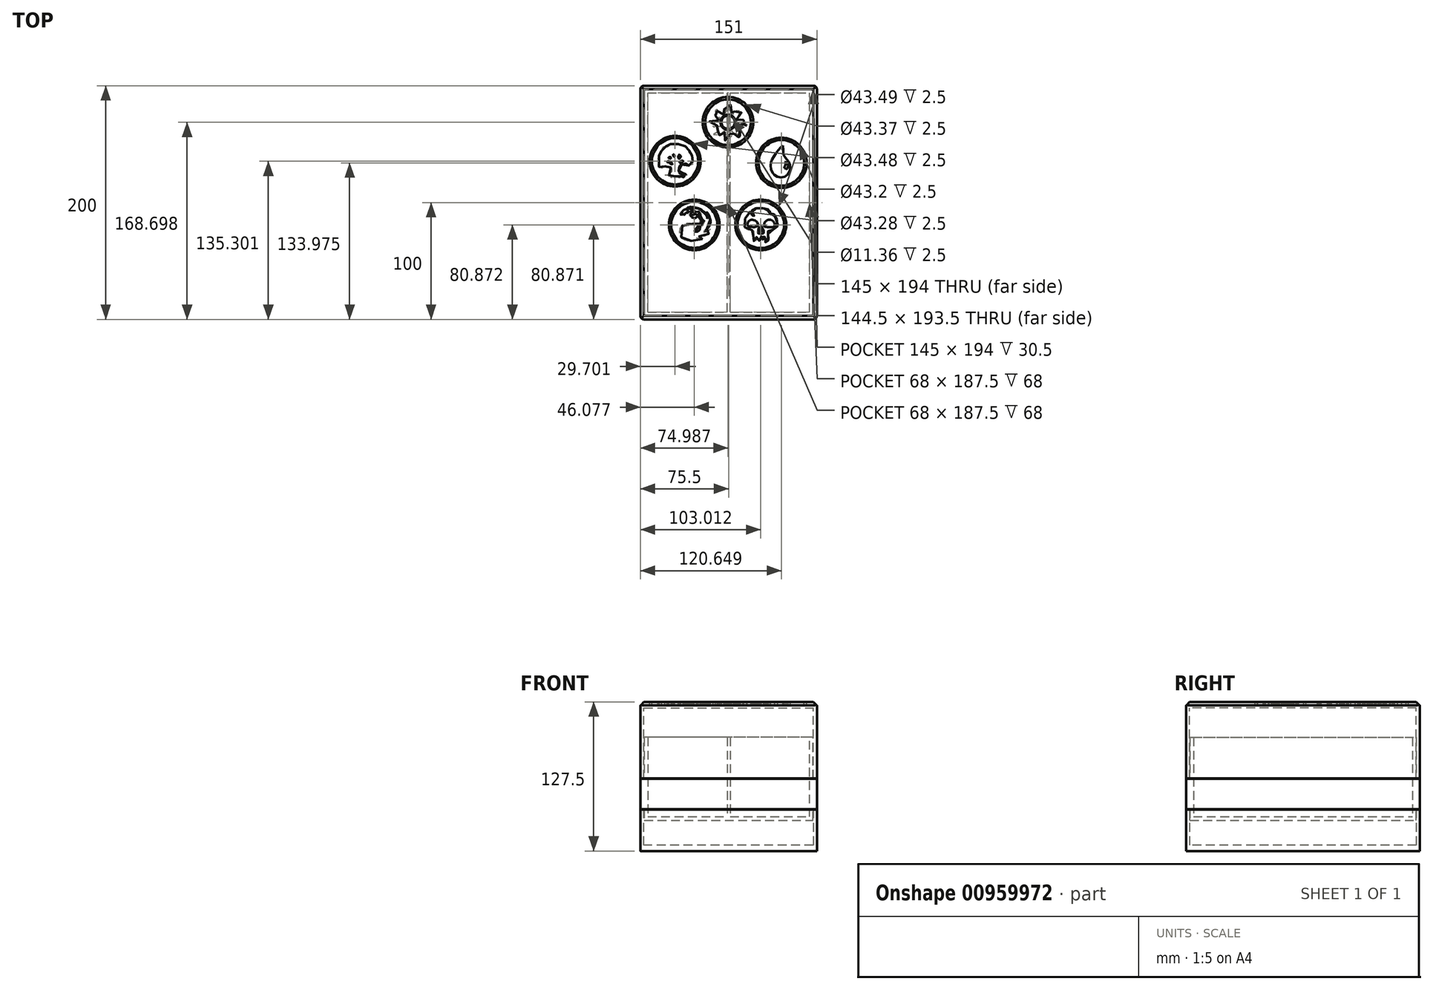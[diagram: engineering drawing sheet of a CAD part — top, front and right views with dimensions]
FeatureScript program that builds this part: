
annotation { "Feature Type Name" : "Feature", "Feature Type Description" : "" }
export const myFeature = defineFeature(function(context is Context, id is Id, definition is map)
    precondition{}
    {
        {
            var Q0;
            Q0=qCreatedBy(makeId("Front.planeOp"),FACE);
            var sketch = newSketch(context, id + "F0", { "sketchPlane" : qUnion([Q0])});
            skLineSegment(sketch, "E0.bottom", {"start": v(-69.25, 34) * mm, "end": v(-1.25, 34) * mm, "construction": true});
            skLineSegment(sketch, "E0.top", {"start": v(-69.25, -34) * mm, "end": v(-1.25, -34) * mm});
            skLineSegment(sketch, "E0.left", {"start": v(-69.25, 34) * mm, "end": v(-69.25, -34) * mm});
            skLineSegment(sketch, "E0.right", {"start": v(-1.25, 34) * mm, "end": v(-1.25, -34) * mm});
            skLineSegment(sketch, "E1", {"start": v(-1.25, -34) * mm, "end": v(1.25, -34) * mm, "construction": true});
            skLineSegment(sketch, "E2", {"start": v(1.25, -34) * mm, "end": v(69.25, -34) * mm});
            skLineSegment(sketch, "E3", {"start": v(69.25, -34) * mm, "end": v(69.25, 34) * mm});
            skLineSegment(sketch, "E4", {"start": v(69.25, 34) * mm, "end": v(1.25, 34) * mm, "construction": true});
            skLineSegment(sketch, "E5", {"start": v(1.25, 34) * mm, "end": v(-1.25, 34) * mm});
            skLineSegment(sketch, "E6", {"start": v(1.25, 34) * mm, "end": v(1.25, -34) * mm});
            skLineSegment(sketch, "E7", {"start": v(1.25, 0) * mm, "end": v(-1.25, 0) * mm, "construction": true});
            skPoint(sketch, "E8", {"position": v(0, 0) * mm});
            skLineSegment(sketch, "E9", {"start": v(-69.25, 34) * mm, "end": v(-72.25, 34) * mm});
            skLineSegment(sketch, "E10", {"start": v(-72.25, 34) * mm, "end": v(-72.25, -1.5) * mm});
            skLineSegment(sketch, "E11", {"start": v(-72.25, -37) * mm, "end": v(72.25, -37) * mm});
            skLineSegment(sketch, "E12", {"start": v(72.25, -37) * mm, "end": v(72.25, -27.5) * mm});
            skLineSegment(sketch, "E13", {"start": v(72.25, 34) * mm, "end": v(69.25, 34) * mm});
            skLineSegment(sketch, "E14", {"start": v(-72.25, -1.5) * mm, "end": v(-69.25, -1.5) * mm, "construction": true});
            skLineSegment(sketch, "E15", {"start": v(-72.25, -1.5) * mm, "end": v(-75.5, -1.5) * mm});
            skLineSegment(sketch, "E16", {"start": v(-75.5, -1.5) * mm, "end": v(-75.5, -27.5) * mm});
            skLineSegment(sketch, "E17", {"start": v(-75.5, -27.5) * mm, "end": v(-72.25, -27.5) * mm});
            skLineSegment(sketch, "E18", {"start": v(72.25, -1.5) * mm, "end": v(75.5, -1.5) * mm});
            skLineSegment(sketch, "E19", {"start": v(75.5, -1.5) * mm, "end": v(75.5, -27.5) * mm});
            skLineSegment(sketch, "E20", {"start": v(75.5, -27.5) * mm, "end": v(72.25, -27.5) * mm});
            skLineSegment(sketch, "E21.trimOffspring", {"start": v(72.25, -1.5) * mm, "end": v(72.25, 34) * mm});
            skLineSegment(sketch, "E22.trimOffspring", {"start": v(-72.25, -27.5) * mm, "end": v(-72.25, -37) * mm});
            skLineSegment(sketch, "E23", {"start": v(72.25, -1.5) * mm, "end": v(72.25, -27.5) * mm, "construction": true});
            skPoint(sketch, "E24", {"position": v(69.25, -1.5) * mm});
            skLineSegment(sketch, "E25", {"start": v(69.25, -1.5) * mm, "end": v(72.25, -1.5) * mm, "construction": true});
            skSolve(sketch);
        }
        {
            var Q0;
            Q0=makeQuery(id+"F0.imprint","IMPRINT",FACE,{"disambiguationData":[TD([[makeQuery(id+"F0.imprint","IMPRINT",EDGE,{"derivedFrom":sQuery(id+"F0.wireOp",EDGE,"E0.top")}),-1.0]])]});
            extrude(context, id + "F1", {"entities" : qUnion([Q0]), "depth" : 187.5 * mm, "offsetDistance" : 25 * mm});
        }
        {
            var Q0;
            Q0=makeQuery(id+"F1.opExtrude","CAP_FACE",FACE,{"disambiguationData":[OSD([sQuery(id+"F0.wireOp",EDGE,"E0.top"),sQuery(id+"F0.wireOp",EDGE,"E0.left"),sQuery(id+"F0.wireOp",EDGE,"E0.right"),sQuery(id+"F0.wireOp",EDGE,"E2"),sQuery(id+"F0.wireOp",EDGE,"E3"),sQuery(id+"F0.wireOp",EDGE,"E5"),sQuery(id+"F0.wireOp",EDGE,"E6"),sQuery(id+"F0.wireOp",EDGE,"E9"),sQuery(id+"F0.wireOp",EDGE,"E10"),sQuery(id+"F0.wireOp",EDGE,"E11"),sQuery(id+"F0.wireOp",EDGE,"E12"),sQuery(id+"F0.wireOp",EDGE,"E13"),sQuery(id+"F0.wireOp",EDGE,"E15"),sQuery(id+"F0.wireOp",EDGE,"E16"),sQuery(id+"F0.wireOp",EDGE,"E17"),sQuery(id+"F0.wireOp",EDGE,"E18"),sQuery(id+"F0.wireOp",EDGE,"E19"),sQuery(id+"F0.wireOp",EDGE,"E20"),sQuery(id+"F0.wireOp",EDGE,"E21.trimOffspring"),sQuery(id+"F0.wireOp",EDGE,"E22.trimOffspring")])],"isStart":false});
            var sketch = newSketch(context, id + "F2", { "sketchPlane" : qUnion([Q0])});
            skLineSegment(sketch, "E26", {"start": v(-69.25, 34) * mm, "end": v(-1.25, 34) * mm});
            skLineSegment(sketch, "E27", {"start": v(1.25, 34) * mm, "end": v(69.25, 34) * mm});
            skSolve(sketch);
        }
        {
            var Q0;
            Q0=makeQuery(id+"F2.imprint","IMPRINT",FACE,{"disambiguationData":[TD([[makeQuery(id+"F2.imprint","IMPRINT",EDGE,{"derivedFrom":makeQuery(id+"F1.opExtrude","CAP_EDGE",EDGE,{"disambiguationData":[OSD([sQuery(id+"F0.wireOp",EDGE,"E0.top")])],"isStart":false})}),-1.0]])]});
            var Q1;
            Q1=makeQuery(id+"F2.imprint","IMPRINT",FACE,{"disambiguationData":[TD([[makeQuery(id+"F2.imprint","IMPRINT",EDGE,{"derivedFrom":sQuery(id+"F2.wireOp",EDGE,"E26")}),-1.0]])]});
            var Q2;
            Q2=makeQuery(id+"F2.imprint","IMPRINT",FACE,{"disambiguationData":[TD([[makeQuery(id+"F2.imprint","IMPRINT",EDGE,{"derivedFrom":sQuery(id+"F2.wireOp",EDGE,"E27")}),-1.0]])]});
            extrude(context, id + "F3", {"entities" : qUnion([Q0, Q1, Q2]), "operationType" : NewBodyOperationType.ADD, "depth" : 3 * mm, "offsetDistance" : 25 * mm});
        }
        {
            var Q0;
            Q0=makeQuery(id+"F0.imprint","IMPRINT",FACE,{"disambiguationData":[TD([[makeQuery(id+"F0.imprint","IMPRINT",EDGE,{"derivedFrom":sQuery(id+"F0.wireOp",EDGE,"E0.top")}),-1.0]])]});
            var sketch = newSketch(context, id + "F4", { "sketchPlane" : qUnion([Q0])});
            skLineSegment(sketch, "E28.0.0", {"start": v(75.5, -27.5) * mm, "end": v(75.5, -1.5) * mm});
            skLineSegment(sketch, "E28.0.1", {"start": v(75.5, -1.5) * mm, "end": v(72.25, -1.5) * mm});
            skLineSegment(sketch, "E28.0.2", {"start": v(72.25, -1.5) * mm, "end": v(72.25, 34) * mm});
            skLineSegment(sketch, "E28.0.3", {"start": v(72.25, 34) * mm, "end": v(69.25, 34) * mm});
            skLineSegment(sketch, "E28.0.4", {"start": v(69.25, 34) * mm, "end": v(69.25, -34) * mm});
            skLineSegment(sketch, "E28.0.5", {"start": v(69.25, -34) * mm, "end": v(1.25, -34) * mm});
            skLineSegment(sketch, "E28.0.6", {"start": v(1.25, -34) * mm, "end": v(1.25, 34) * mm});
            skLineSegment(sketch, "E28.0.7", {"start": v(1.25, 34) * mm, "end": v(-1.25, 34) * mm});
            skLineSegment(sketch, "E28.0.8", {"start": v(-1.25, 34) * mm, "end": v(-1.25, -34) * mm});
            skLineSegment(sketch, "E28.0.9", {"start": v(-1.25, -34) * mm, "end": v(-69.25, -34) * mm});
            skLineSegment(sketch, "E28.0.10", {"start": v(-69.25, -34) * mm, "end": v(-69.25, 34) * mm});
            skLineSegment(sketch, "E28.0.11", {"start": v(-69.25, 34) * mm, "end": v(-72.25, 34) * mm});
            skLineSegment(sketch, "E28.0.12", {"start": v(-72.25, 34) * mm, "end": v(-72.25, -1.5) * mm});
            skLineSegment(sketch, "E28.0.13", {"start": v(-72.25, -1.5) * mm, "end": v(-75.5, -1.5) * mm});
            skLineSegment(sketch, "E28.0.14", {"start": v(-75.5, -1.5) * mm, "end": v(-75.5, -27.5) * mm});
            skLineSegment(sketch, "E28.0.15", {"start": v(-75.5, -27.5) * mm, "end": v(-72.25, -27.5) * mm});
            skLineSegment(sketch, "E28.0.16", {"start": v(-72.25, -27.5) * mm, "end": v(-72.25, -37) * mm});
            skLineSegment(sketch, "E28.0.17", {"start": v(-72.25, -37) * mm, "end": v(72.25, -37) * mm});
            skLineSegment(sketch, "E28.0.18", {"start": v(72.25, -37) * mm, "end": v(72.25, -27.5) * mm});
            skLineSegment(sketch, "E28.0.19", {"start": v(72.25, -27.5) * mm, "end": v(75.5, -27.5) * mm});
            skLineSegment(sketch, "E29", {"start": v(69.25, 34) * mm, "end": v(1.25, 34) * mm});
            skLineSegment(sketch, "E30", {"start": v(-1.25, 34) * mm, "end": v(-69.25, 34) * mm});
            skSolve(sketch);
        }
        {
            var Q0;
            Q0=makeQuery(id+"F0.imprint","IMPRINT",FACE,{"disambiguationData":[TD([[makeQuery(id+"F0.imprint","IMPRINT",EDGE,{"derivedFrom":sQuery(id+"F0.wireOp",EDGE,"E0.top")}),-1.0]])]});
            var Q1;
            Q1=makeQuery(id+"F4.imprint","IMPRINT",FACE,{"disambiguationData":[TD([[makeQuery(id+"F4.imprint","IMPRINT",EDGE,{"derivedFrom":sQuery(id+"F4.wireOp",EDGE,"E28.0.4")}),1.0]])]});
            var Q2;
            Q2=makeQuery(id+"F4.imprint","IMPRINT",FACE,{"disambiguationData":[TD([[makeQuery(id+"F4.imprint","IMPRINT",EDGE,{"derivedFrom":sQuery(id+"F4.wireOp",EDGE,"E28.0.8")}),-1.0]])]});
            extrude(context, id + "F5", {"entities" : qUnion([Q0, Q1, Q2]), "operationType" : NewBodyOperationType.ADD, "oppositeDirection" : true, "depth" : 3 * mm, "offsetDistance" : 25 * mm});
        }
        {
            var Q0;
            {var subQ0=sQuery(id+"F0.wireOp",EDGE,"E18");Q0=makeQuery(id+"F5.boolean.opBoolean","MERGE",FACE,{"derivedFrom":[makeQuery(id+"F3.boolean.opBoolean","MERGE",FACE,{"derivedFrom":[makeQuery(id+"F1.opExtrude","SWEPT_FACE",FACE,{"disambiguationData":[OSD([subQ0])]}),makeQuery(id+"F3.opExtrude","SWEPT_FACE",FACE,{"disambiguationData":[OSD([subQ0])]})]}),makeQuery(id+"F5.opExtrude","SWEPT_FACE",FACE,{"disambiguationData":[OSD([subQ0])]})]});}
            var sketch = newSketch(context, id + "F6", { "sketchPlane" : qUnion([Q0])});
            skLineSegment(sketch, "E31.0.0", {"start": v(72.25, 3) * mm, "end": v(-72.25, 3) * mm});
            skLineSegment(sketch, "E31.0.1", {"start": v(-72.25, 3) * mm, "end": v(-72.25, -190.5) * mm});
            skLineSegment(sketch, "E31.0.2", {"start": v(-72.25, -190.5) * mm, "end": v(72.25, -190.5) * mm});
            skLineSegment(sketch, "E31.0.3", {"start": v(72.25, -190.5) * mm, "end": v(72.25, 3) * mm});
            skLineSegment(sketch, "E32.0.0", {"start": v(75.5, -190.5) * mm, "end": v(75.5, 3) * mm});
            skLineSegment(sketch, "E32.0.1", {"start": v(75.5, 3) * mm, "end": v(72.25, 3) * mm});
            skLineSegment(sketch, "E32.0.2", {"start": v(72.25, 3) * mm, "end": v(72.25, -190.5) * mm});
            skLineSegment(sketch, "E32.0.3", {"start": v(72.25, -190.5) * mm, "end": v(75.5, -190.5) * mm});
            skLineSegment(sketch, "E33.0.0", {"start": v(-72.25, -190.5) * mm, "end": v(-72.25, 3) * mm});
            skLineSegment(sketch, "E33.0.1", {"start": v(-72.25, 3) * mm, "end": v(-75.5, 3) * mm});
            skLineSegment(sketch, "E33.0.2", {"start": v(-75.5, 3) * mm, "end": v(-75.5, -190.5) * mm});
            skLineSegment(sketch, "E33.0.3", {"start": v(-75.5, -190.5) * mm, "end": v(-72.25, -190.5) * mm});
            skLineSegment(sketch, "E34", {"start": v(75.5, 3) * mm, "end": v(75.5, 6.25) * mm});
            skLineSegment(sketch, "E35", {"start": v(75.5, 6.25) * mm, "end": v(-75.5, 6.25) * mm});
            skLineSegment(sketch, "E36", {"start": v(-75.5, 6.25) * mm, "end": v(-75.5, 3) * mm});
            skLineSegment(sketch, "E37", {"start": v(75.5, -190.5) * mm, "end": v(75.5, -193.75) * mm});
            skLineSegment(sketch, "E38", {"start": v(75.5, -193.75) * mm, "end": v(-75.5, -193.75) * mm});
            skLineSegment(sketch, "E39", {"start": v(-75.5, -193.75) * mm, "end": v(-75.5, -190.5) * mm});
            skSolve(sketch);
        }
        {
            var Q0;
            Q0=makeQuery(id+"F6.imprint","IMPRINT",FACE,{"disambiguationData":[TD([[makeQuery(id+"F6.imprint","IMPRINT",EDGE,{"derivedFrom":sQuery(id+"F6.wireOp",EDGE,"E31.0.0")}),-1.0]])]});
            var Q1;
            Q1=makeQuery(id+"F6.imprint","IMPRINT",FACE,{"disambiguationData":[TD([[makeQuery(id+"F6.imprint","IMPRINT",EDGE,{"derivedFrom":sQuery(id+"F6.wireOp",EDGE,"E31.0.2")}),-1.0]])]});
            extrude(context, id + "F7", {"entities" : qUnion([Q0, Q1]), "operationType" : NewBodyOperationType.ADD, "oppositeDirection" : true, "depth" : 26 * mm, "offsetDistance" : 25 * mm});
        }
        {
            var Q0;
            {var subQ0=sQuery(id+"F0.wireOp",EDGE,"E18");var subQ1=sQuery(id+"F0.wireOp",EDGE,"E5");var subQ2=sQuery(id+"F0.wireOp",EDGE,"E15");var subQ3=sQuery(id+"F0.wireOp",EDGE,"E10");var subQ4=sQuery(id+"F0.wireOp",EDGE,"E9");var subQ5=sQuery(id+"F0.wireOp",EDGE,"E21.trimOffspring");var subQ6=sQuery(id+"F0.wireOp",EDGE,"E13");var subQ7=sQuery(id+"F2.wireOp",EDGE,"E27");var subQ8=sQuery(id+"F2.wireOp",EDGE,"E26");Q0=makeQuery(id+"F7.boolean.opBoolean","SPLIT",FACE,{"disambiguationData":[TD([makeQuery(id+"F1.opExtrude","SWEPT_FACE",FACE,{"disambiguationData":[OSD([subQ1])]})])],"derivedFrom":makeQuery(id+"F3.opExtrude","CAP_FACE",FACE,{"disambiguationData":[OSD([subQ1,subQ4,subQ3,sQuery(id+"F0.wireOp",EDGE,"E11"),sQuery(id+"F0.wireOp",EDGE,"E12"),subQ6,subQ2,sQuery(id+"F0.wireOp",EDGE,"E16"),sQuery(id+"F0.wireOp",EDGE,"E17"),subQ0,sQuery(id+"F0.wireOp",EDGE,"E19"),sQuery(id+"F0.wireOp",EDGE,"E20"),subQ5,sQuery(id+"F0.wireOp",EDGE,"E22.trimOffspring"),subQ8,subQ7])],"isStart":false})});}
            var sketch = newSketch(context, id + "F8", { "sketchPlane" : qUnion([Q0])});
            skLineSegment(sketch, "E40.0.0", {"start": v(75.5, -1.5) * mm, "end": v(-75.5, -1.5) * mm});
            skLineSegment(sketch, "E40.0.1", {"start": v(-75.5, -1.5) * mm, "end": v(-75.5, -27.5) * mm});
            skLineSegment(sketch, "E40.0.2", {"start": v(-75.5, -27.5) * mm, "end": v(75.5, -27.5) * mm});
            skLineSegment(sketch, "E40.0.3", {"start": v(75.5, -27.5) * mm, "end": v(75.5, -1.5) * mm});
            skLineSegment(sketch, "E41.0.0", {"start": v(-72.25, 34) * mm, "end": v(-72.25, -1.5) * mm});
            skLineSegment(sketch, "E41.0.1", {"start": v(-72.25, -1.5) * mm, "end": v(72.25, -1.5) * mm});
            skLineSegment(sketch, "E41.0.2", {"start": v(72.25, -1.5) * mm, "end": v(72.25, 34) * mm});
            skLineSegment(sketch, "E41.0.3", {"start": v(72.25, 34) * mm, "end": v(-72.25, 34) * mm});
            skLineSegment(sketch, "E42", {"start": v(72.25, 34) * mm, "end": v(72.25, 59.25) * mm, "construction": true});
            skLineSegment(sketch, "E43", {"start": v(75.5, -1.5) * mm, "end": v(75.5, -1.25) * mm, "construction": true});
            skLineSegment(sketch, "E44", {"start": v(75.5, -1.25) * mm, "end": v(72.5, -1.25) * mm});
            skLineSegment(sketch, "E45", {"start": v(72.5, -1.25) * mm, "end": v(72.5, 59.25) * mm});
            skLineSegment(sketch, "E46", {"start": v(72.5, 59.25) * mm, "end": v(75.5, 59.25) * mm, "construction": true});
            skLineSegment(sketch, "E47", {"start": v(75.5, 59.25) * mm, "end": v(75.5, -1.25) * mm});
            skLineSegment(sketch, "E48", {"start": v(-75.5, -1.5) * mm, "end": v(-75.5, -1.25) * mm, "construction": true});
            skLineSegment(sketch, "E49", {"start": v(-75.5, -1.25) * mm, "end": v(-72.5, -1.25) * mm});
            skLineSegment(sketch, "E50", {"start": v(-72.5, -1.25) * mm, "end": v(-72.5, 59.25) * mm});
            skLineSegment(sketch, "E51", {"start": v(-72.5, 59.25) * mm, "end": v(-75.5, 59.25) * mm, "construction": true});
            skLineSegment(sketch, "E52", {"start": v(-75.5, 59.25) * mm, "end": v(-75.5, -1.25) * mm});
            skLineSegment(sketch, "E53", {"start": v(-72.5, 59.25) * mm, "end": v(72.5, 59.25) * mm});
            skLineSegment(sketch, "E54", {"start": v(75.5, 59.25) * mm, "end": v(75.5, 64.25) * mm});
            skLineSegment(sketch, "E55", {"start": v(75.5, 64.25) * mm, "end": v(-75.5, 64.25) * mm});
            skLineSegment(sketch, "E56", {"start": v(-75.5, 64.25) * mm, "end": v(-75.5, 59.25) * mm});
            skSolve(sketch);
        }
        {
            var Q0;
            Q0=makeQuery(id+"F8.imprint","IMPRINT",FACE,{"disambiguationData":[TD([[makeQuery(id+"F8.imprint","IMPRINT",EDGE,{"derivedFrom":sQuery(id+"F8.wireOp",EDGE,"E44")}),-1.0]])]});
            extrude(context, id + "F9", {"entities" : qUnion([Q0]), "oppositeDirection" : true, "depth" : 193.75 * mm, "offsetDistance" : 25 * mm, "hasSecondDirection" : true, "secondDirectionOppositeDirection" : false, "secondDirectionDepth" : .25 * mm});
        }
        {
            var Q0;
            Q0=makeQuery(id+"F9.opExtrude","CAP_FACE",FACE,{"disambiguationData":[OSD([sQuery(id+"F8.wireOp",EDGE,"E44"),sQuery(id+"F8.wireOp",EDGE,"E45"),sQuery(id+"F8.wireOp",EDGE,"E47"),sQuery(id+"F8.wireOp",EDGE,"E49"),sQuery(id+"F8.wireOp",EDGE,"E50"),sQuery(id+"F8.wireOp",EDGE,"E52"),sQuery(id+"F8.wireOp",EDGE,"E53"),sQuery(id+"F8.wireOp",EDGE,"E54"),sQuery(id+"F8.wireOp",EDGE,"E55"),sQuery(id+"F8.wireOp",EDGE,"E56")])],"isStart":false});
            var sketch = newSketch(context, id + "F10", { "sketchPlane" : qUnion([Q0])});
            skLineSegment(sketch, "E57.0.0", {"start": v(75.5, -1.25) * mm, "end": v(75.5, 64.25) * mm});
            skLineSegment(sketch, "E57.0.1", {"start": v(75.5, 64.25) * mm, "end": v(-75.5, 64.25) * mm});
            skLineSegment(sketch, "E57.0.2", {"start": v(-75.5, 64.25) * mm, "end": v(-75.5, -1.25) * mm});
            skLineSegment(sketch, "E57.0.3", {"start": v(-75.5, -1.25) * mm, "end": v(-72.5, -1.25) * mm});
            skLineSegment(sketch, "E57.0.4", {"start": v(-72.5, -1.25) * mm, "end": v(-72.5, 59.25) * mm});
            skLineSegment(sketch, "E57.0.5", {"start": v(-72.5, 59.25) * mm, "end": v(72.5, 59.25) * mm});
            skLineSegment(sketch, "E57.0.6", {"start": v(72.5, 59.25) * mm, "end": v(72.5, -1.25) * mm});
            skLineSegment(sketch, "E57.0.7", {"start": v(72.5, -1.25) * mm, "end": v(75.5, -1.25) * mm});
            skLineSegment(sketch, "E58.bottom", {"start": v(-75.5, 64.25) * mm, "end": v(75.5, 64.25) * mm});
            skLineSegment(sketch, "E58.top", {"start": v(-75.5, -1.25) * mm, "end": v(75.5, -1.25) * mm});
            skLineSegment(sketch, "E58.right", {"start": v(75.5, 64.25) * mm, "end": v(75.5, -1.25) * mm});
            skSolve(sketch);
        }
        {
            var Q0;
            Q0=makeQuery(id+"F10.imprint","IMPRINT",FACE,{"disambiguationData":[TD([[makeQuery(id+"F10.imprint","IMPRINT",EDGE,{"derivedFrom":sQuery(id+"F10.wireOp",EDGE,"E57.0.4")}),-1.0]])]});
            var Q1;
            Q1=makeQuery(id+"F10.imprint","IMPRINT",FACE,{"disambiguationData":[TD([[makeQuery(id+"F10.imprint","IMPRINT",EDGE,{"derivedFrom":sQuery(id+"F10.wireOp",EDGE,"E57.0.0")}),-1.0]])]});
            extrude(context, id + "F11", {"entities" : qUnion([Q0, Q1]), "operationType" : NewBodyOperationType.ADD, "depth" : 3 * mm, "offsetDistance" : 25 * mm});
        }
        {
            var Q0;
            Q0=makeQuery(id+"F9.opExtrude","CAP_FACE",FACE,{"disambiguationData":[OSD([sQuery(id+"F8.wireOp",EDGE,"E44"),sQuery(id+"F8.wireOp",EDGE,"E45"),sQuery(id+"F8.wireOp",EDGE,"E47"),sQuery(id+"F8.wireOp",EDGE,"E49"),sQuery(id+"F8.wireOp",EDGE,"E50"),sQuery(id+"F8.wireOp",EDGE,"E52"),sQuery(id+"F8.wireOp",EDGE,"E53"),sQuery(id+"F8.wireOp",EDGE,"E54"),sQuery(id+"F8.wireOp",EDGE,"E55"),sQuery(id+"F8.wireOp",EDGE,"E56")])],"isStart":true});
            var sketch = newSketch(context, id + "F12", { "sketchPlane" : qUnion([Q0])});
            skLineSegment(sketch, "E59.0.0", {"start": v(-75.5, 64.25) * mm, "end": v(-75.5, -1.25) * mm});
            skLineSegment(sketch, "E59.0.1", {"start": v(-75.5, -1.25) * mm, "end": v(-72.5, -1.25) * mm});
            skLineSegment(sketch, "E59.0.2", {"start": v(-72.5, -1.25) * mm, "end": v(-72.5, 59.25) * mm});
            skLineSegment(sketch, "E59.0.3", {"start": v(-72.5, 59.25) * mm, "end": v(72.5, 59.25) * mm});
            skLineSegment(sketch, "E59.0.4", {"start": v(72.5, 59.25) * mm, "end": v(72.5, -1.25) * mm});
            skLineSegment(sketch, "E59.0.5", {"start": v(72.5, -1.25) * mm, "end": v(75.5, -1.25) * mm});
            skLineSegment(sketch, "E59.0.6", {"start": v(75.5, -1.25) * mm, "end": v(75.5, 64.25) * mm});
            skLineSegment(sketch, "E59.0.7", {"start": v(75.5, 64.25) * mm, "end": v(-75.5, 64.25) * mm});
            skLineSegment(sketch, "E60.bottom", {"start": v(-75.5, 64.25) * mm, "end": v(75.5, 64.25) * mm});
            skLineSegment(sketch, "E60.top", {"start": v(-75.5, -1.25) * mm, "end": v(75.5, -1.25) * mm});
            skLineSegment(sketch, "E60.right", {"start": v(75.5, 64.25) * mm, "end": v(75.5, -1.25) * mm});
            skSolve(sketch);
        }
        {
            var Q0;
            Q0=makeQuery(id+"F12.imprint","IMPRINT",FACE,{"disambiguationData":[TD([[makeQuery(id+"F12.imprint","IMPRINT",EDGE,{"derivedFrom":sQuery(id+"F12.wireOp",EDGE,"E59.0.2")}),-1.0]])]});
            var Q1;
            Q1=makeQuery(id+"F12.imprint","IMPRINT",FACE,{"disambiguationData":[TD([[makeQuery(id+"F12.imprint","IMPRINT",EDGE,{"derivedFrom":sQuery(id+"F12.wireOp",EDGE,"E59.0.0")}),1.0]])]});
            extrude(context, id + "F13", {"entities" : qUnion([Q0, Q1]), "operationType" : NewBodyOperationType.ADD, "depth" : 3 * mm, "offsetDistance" : 25 * mm});
        }
        {
            var Q0;
            Q0=makeQuery(id+"F13.boolean.opBoolean","MERGE",FACE,{"derivedFrom":[makeQuery(id+"F11.boolean.opBoolean","MERGE",FACE,{"derivedFrom":[makeQuery(id+"F9.opExtrude","SWEPT_FACE",FACE,{"disambiguationData":[OSD([sQuery(id+"F8.wireOp",EDGE,"E55")])]}),makeQuery(id+"F11.opExtrude","SWEPT_FACE",FACE,{"disambiguationData":[OSD([sQuery(id+"F10.wireOp",EDGE,"E57.0.1")])]})]}),makeQuery(id+"F13.opExtrude","SWEPT_FACE",FACE,{"disambiguationData":[OSD([sQuery(id+"F12.wireOp",EDGE,"E59.0.7")])]})]});
            chamfer(context, id + "F14", {"entities" : qUnion([Q0]), "width" : 3 * mm, "tangentPropagation" : true});
        }
        {
            var Q0;
            Q0=makeQuery(id+"F13.opExtrude","CAP_EDGE",EDGE,{"disambiguationData":[OSD([sQuery(id+"F12.wireOp",EDGE,"E59.0.6")])],"isStart":false});
            var Q1;
            Q1=makeQuery(id+"F11.opExtrude","CAP_EDGE",EDGE,{"disambiguationData":[OSD([sQuery(id+"F10.wireOp",EDGE,"E57.0.2")])],"isStart":false});
            var Q2;
            Q2=makeQuery(id+"F13.opExtrude","CAP_EDGE",EDGE,{"disambiguationData":[OSD([sQuery(id+"F12.wireOp",EDGE,"E59.0.0")])],"isStart":false});
            var Q3;
            Q3=makeQuery(id+"F11.opExtrude","CAP_EDGE",EDGE,{"disambiguationData":[OSD([sQuery(id+"F10.wireOp",EDGE,"E57.0.0")])],"isStart":false});
            fillet(context, id + "F15", {"entities" : qUnion([Q0, Q1, Q2, Q3]), "radius" : 3 * mm, "tangentPropagation" : true, "allowEdgeOverflow" : false});
        }
        {
            var Q0;
            Q0=makeQuery(id+"F7.opExtrude","SWEPT_EDGE",EDGE,{"disambiguationData":[OSD([sQuery(id+"F6.wireOp",EDGE,"E37"),sQuery(id+"F6.wireOp",EDGE,"E38")])]});
            var Q1;
            Q1=makeQuery(id+"F7.opExtrude","SWEPT_EDGE",EDGE,{"disambiguationData":[OSD([sQuery(id+"F6.wireOp",EDGE,"E34"),sQuery(id+"F6.wireOp",EDGE,"E35")])]});
            var Q2;
            Q2=makeQuery(id+"F7.opExtrude","SWEPT_EDGE",EDGE,{"disambiguationData":[OSD([sQuery(id+"F6.wireOp",EDGE,"E38"),sQuery(id+"F6.wireOp",EDGE,"E39")])]});
            var Q3;
            Q3=makeQuery(id+"F7.opExtrude","SWEPT_EDGE",EDGE,{"disambiguationData":[OSD([sQuery(id+"F6.wireOp",EDGE,"E35"),sQuery(id+"F6.wireOp",EDGE,"E36")])]});
            fillet(context, id + "F16", {"entities" : qUnion([Q0, Q1, Q2, Q3]), "radius" : 3 * mm, "tangentPropagation" : true, "allowEdgeOverflow" : false});
        }
        {
            var Q0;
            {var subQ0=sQuery(id+"F0.wireOp",EDGE,"E20");var subQ1=sQuery(id+"F0.wireOp",EDGE,"E22.trimOffspring");var subQ2=sQuery(id+"F0.wireOp",EDGE,"E17");var subQ3=sQuery(id+"F0.wireOp",EDGE,"E12");var subQ4=sQuery(id+"F0.wireOp",EDGE,"E11");Q0=makeQuery(id+"F7.boolean.opBoolean","SPLIT",FACE,{"disambiguationData":[TD([makeQuery(id+"F1.opExtrude","SWEPT_FACE",FACE,{"disambiguationData":[OSD([subQ4])]})])],"derivedFrom":makeQuery(id+"F3.opExtrude","CAP_FACE",FACE,{"disambiguationData":[OSD([sQuery(id+"F0.wireOp",EDGE,"E5"),sQuery(id+"F0.wireOp",EDGE,"E9"),sQuery(id+"F0.wireOp",EDGE,"E10"),subQ4,subQ3,sQuery(id+"F0.wireOp",EDGE,"E13"),sQuery(id+"F0.wireOp",EDGE,"E15"),sQuery(id+"F0.wireOp",EDGE,"E16"),subQ2,sQuery(id+"F0.wireOp",EDGE,"E18"),sQuery(id+"F0.wireOp",EDGE,"E19"),subQ0,sQuery(id+"F0.wireOp",EDGE,"E21.trimOffspring"),subQ1,sQuery(id+"F2.wireOp",EDGE,"E26"),sQuery(id+"F2.wireOp",EDGE,"E27")])],"isStart":false})});}
            var sketch = newSketch(context, id + "F17", { "sketchPlane" : qUnion([Q0])});
            skLineSegment(sketch, "E61.0.0", {"start": v(72.25, -27.5) * mm, "end": v(-72.25, -27.5) * mm});
            skLineSegment(sketch, "E61.0.1", {"start": v(-72.25, -27.5) * mm, "end": v(-72.25, -37) * mm});
            skLineSegment(sketch, "E61.0.2", {"start": v(-72.25, -37) * mm, "end": v(72.25, -37) * mm});
            skLineSegment(sketch, "E61.0.3", {"start": v(72.25, -37) * mm, "end": v(72.25, -27.5) * mm});
            skLineSegment(sketch, "E62.0.0", {"start": v(-75.5, -27.5) * mm, "end": v(-72.5, -27.5) * mm});
            skLineSegment(sketch, "E62.0.1", {"start": v(-72.5, -1.5) * mm, "end": v(-72.5, -27.5) * mm});
            skLineSegment(sketch, "E62.0.2", {"start": v(-72.5, -1.5) * mm, "end": v(-75.5, -1.5) * mm});
            skLineSegment(sketch, "E62.0.3", {"start": v(-75.5, -1.5) * mm, "end": v(-75.5, -27.5) * mm});
            skLineSegment(sketch, "E63.0.0", {"start": v(72.5, -27.5) * mm, "end": v(75.5, -27.5) * mm});
            skLineSegment(sketch, "E63.0.1", {"start": v(75.5, -1.5) * mm, "end": v(75.5, -27.5) * mm});
            skLineSegment(sketch, "E63.0.2", {"start": v(75.5, -1.5) * mm, "end": v(72.5, -1.5) * mm});
            skLineSegment(sketch, "E63.0.3", {"start": v(72.5, -1.5) * mm, "end": v(72.5, -27.5) * mm});
            skLineSegment(sketch, "E64", {"start": v(-72.25, -37) * mm, "end": v(-72.25, -58.25) * mm, "construction": true});
            skLineSegment(sketch, "E65", {"start": v(-75.5, -27.5) * mm, "end": v(-75.5, -27.75) * mm, "construction": true});
            skLineSegment(sketch, "E66", {"start": v(-75.5, -27.75) * mm, "end": v(-75.5, -58.25) * mm});
            skLineSegment(sketch, "E67", {"start": v(-75.5, -58.25) * mm, "end": v(-72.5, -58.25) * mm, "construction": true});
            skLineSegment(sketch, "E68", {"start": v(-72.5, -58.25) * mm, "end": v(-72.5, -27.75) * mm});
            skLineSegment(sketch, "E69", {"start": v(-72.5, -27.75) * mm, "end": v(-75.5, -27.75) * mm});
            skLineSegment(sketch, "E70", {"start": v(72.5, -27.5) * mm, "end": v(72.5, -27.75) * mm, "construction": true});
            skLineSegment(sketch, "E71", {"start": v(72.5, -27.75) * mm, "end": v(72.5, -58.25) * mm});
            skLineSegment(sketch, "E72", {"start": v(72.5, -58.25) * mm, "end": v(75.5, -58.25) * mm, "construction": true});
            skLineSegment(sketch, "E73", {"start": v(75.5, -58.25) * mm, "end": v(75.5, -27.75) * mm});
            skLineSegment(sketch, "E74", {"start": v(75.5, -27.75) * mm, "end": v(72.5, -27.75) * mm});
            skLineSegment(sketch, "E75", {"start": v(-75.5, -58.25) * mm, "end": v(-75.5, -63.25) * mm});
            skLineSegment(sketch, "E76", {"start": v(-75.5, -63.25) * mm, "end": v(75.5, -63.25) * mm});
            skLineSegment(sketch, "E77", {"start": v(75.5, -63.25) * mm, "end": v(75.5, -58.25) * mm});
            skLineSegment(sketch, "E78", {"start": v(72.5, -58.25) * mm, "end": v(-72.5, -58.25) * mm});
            skSolve(sketch);
        }
        {
            var Q0;
            Q0=makeQuery(id+"F17.imprint","IMPRINT",FACE,{"disambiguationData":[TD([[makeQuery(id+"F17.imprint","IMPRINT",EDGE,{"derivedFrom":sQuery(id+"F17.wireOp",EDGE,"E66")}),1.0]])]});
            extrude(context, id + "F18", {"entities" : qUnion([Q0]), "oppositeDirection" : true, "depth" : 193.75 * mm, "offsetDistance" : 25 * mm, "hasSecondDirection" : true, "secondDirectionOppositeDirection" : false, "secondDirectionDepth" : .25 * mm});
        }
        {
            var Q0;
            Q0=makeQuery(id+"F18.opExtrude","CAP_FACE",FACE,{"disambiguationData":[OSD([sQuery(id+"F17.wireOp",EDGE,"E66"),sQuery(id+"F17.wireOp",EDGE,"E68"),sQuery(id+"F17.wireOp",EDGE,"E69"),sQuery(id+"F17.wireOp",EDGE,"E71"),sQuery(id+"F17.wireOp",EDGE,"E73"),sQuery(id+"F17.wireOp",EDGE,"E74"),sQuery(id+"F17.wireOp",EDGE,"E75"),sQuery(id+"F17.wireOp",EDGE,"E76"),sQuery(id+"F17.wireOp",EDGE,"E77"),sQuery(id+"F17.wireOp",EDGE,"E78")])],"isStart":true});
            var sketch = newSketch(context, id + "F19", { "sketchPlane" : qUnion([Q0])});
            skLineSegment(sketch, "E79.0.0", {"start": v(75.5, -27.75) * mm, "end": v(72.5, -27.75) * mm});
            skLineSegment(sketch, "E79.0.1", {"start": v(72.5, -27.75) * mm, "end": v(72.5, -58.25) * mm});
            skLineSegment(sketch, "E79.0.2", {"start": v(72.5, -58.25) * mm, "end": v(-72.5, -58.25) * mm});
            skLineSegment(sketch, "E79.0.3", {"start": v(-72.5, -58.25) * mm, "end": v(-72.5, -27.75) * mm});
            skLineSegment(sketch, "E79.0.4", {"start": v(-72.5, -27.75) * mm, "end": v(-75.5, -27.75) * mm});
            skLineSegment(sketch, "E79.0.5", {"start": v(-75.5, -27.75) * mm, "end": v(-75.5, -63.25) * mm});
            skLineSegment(sketch, "E79.0.6", {"start": v(-75.5, -63.25) * mm, "end": v(75.5, -63.25) * mm});
            skLineSegment(sketch, "E79.0.7", {"start": v(75.5, -63.25) * mm, "end": v(75.5, -27.75) * mm});
            skLineSegment(sketch, "E80.bottom", {"start": v(-75.5, -27.75) * mm, "end": v(75.5, -27.75) * mm});
            skLineSegment(sketch, "E80.right", {"start": v(75.5, -27.75) * mm, "end": v(75.5, -63.25) * mm});
            skSolve(sketch);
        }
        {
            var Q0;
            Q0=makeQuery(id+"F19.imprint","IMPRINT",FACE,{"disambiguationData":[TD([[makeQuery(id+"F19.imprint","IMPRINT",EDGE,{"derivedFrom":sQuery(id+"F19.wireOp",EDGE,"E79.0.1")}),-1.0]])]});
            var Q1;
            Q1=makeQuery(id+"F19.imprint","IMPRINT",FACE,{"disambiguationData":[TD([[makeQuery(id+"F19.imprint","IMPRINT",EDGE,{"derivedFrom":sQuery(id+"F19.wireOp",EDGE,"E79.0.0")}),1.0]])]});
            extrude(context, id + "F20", {"entities" : qUnion([Q0, Q1]), "operationType" : NewBodyOperationType.ADD, "depth" : 3 * mm, "offsetDistance" : 25 * mm});
        }
        {
            var Q0;
            Q0=makeQuery(id+"F18.opExtrude","CAP_FACE",FACE,{"disambiguationData":[OSD([sQuery(id+"F17.wireOp",EDGE,"E66"),sQuery(id+"F17.wireOp",EDGE,"E68"),sQuery(id+"F17.wireOp",EDGE,"E69"),sQuery(id+"F17.wireOp",EDGE,"E71"),sQuery(id+"F17.wireOp",EDGE,"E73"),sQuery(id+"F17.wireOp",EDGE,"E74"),sQuery(id+"F17.wireOp",EDGE,"E75"),sQuery(id+"F17.wireOp",EDGE,"E76"),sQuery(id+"F17.wireOp",EDGE,"E77"),sQuery(id+"F17.wireOp",EDGE,"E78")])],"isStart":false});
            var sketch = newSketch(context, id + "F21", { "sketchPlane" : qUnion([Q0])});
            skLineSegment(sketch, "E81.0.0", {"start": v(-72.5, -27.75) * mm, "end": v(-75.5, -27.75) * mm});
            skLineSegment(sketch, "E81.0.1", {"start": v(-75.5, -27.75) * mm, "end": v(-75.5, -63.25) * mm});
            skLineSegment(sketch, "E81.0.2", {"start": v(-75.5, -63.25) * mm, "end": v(75.5, -63.25) * mm});
            skLineSegment(sketch, "E81.0.3", {"start": v(75.5, -63.25) * mm, "end": v(75.5, -27.75) * mm});
            skLineSegment(sketch, "E81.0.4", {"start": v(75.5, -27.75) * mm, "end": v(72.5, -27.75) * mm});
            skLineSegment(sketch, "E81.0.5", {"start": v(72.5, -27.75) * mm, "end": v(72.5, -58.25) * mm});
            skLineSegment(sketch, "E81.0.6", {"start": v(72.5, -58.25) * mm, "end": v(-72.5, -58.25) * mm});
            skLineSegment(sketch, "E81.0.7", {"start": v(-72.5, -58.25) * mm, "end": v(-72.5, -27.75) * mm});
            skLineSegment(sketch, "E82.bottom", {"start": v(-75.5, -27.75) * mm, "end": v(75.5, -27.75) * mm});
            skLineSegment(sketch, "E82.right", {"start": v(75.5, -27.75) * mm, "end": v(75.5, -63.25) * mm});
            skSolve(sketch);
        }
        {
            var Q0;
            Q0=makeQuery(id+"F21.imprint","IMPRINT",FACE,{"disambiguationData":[TD([[makeQuery(id+"F21.imprint","IMPRINT",EDGE,{"derivedFrom":sQuery(id+"F21.wireOp",EDGE,"E81.0.5")}),1.0]])]});
            var Q1;
            Q1=makeQuery(id+"F21.imprint","IMPRINT",FACE,{"disambiguationData":[TD([[makeQuery(id+"F21.imprint","IMPRINT",EDGE,{"derivedFrom":sQuery(id+"F21.wireOp",EDGE,"E81.0.0")}),-1.0]])]});
            extrude(context, id + "F22", {"entities" : qUnion([Q0, Q1]), "operationType" : NewBodyOperationType.ADD, "depth" : 3 * mm, "offsetDistance" : 25 * mm});
        }
        {
            var Q0;
            Q0=makeQuery(id+"F20.opExtrude","CAP_EDGE",EDGE,{"disambiguationData":[OSD([sQuery(id+"F19.wireOp",EDGE,"E79.0.7")])],"isStart":false});
            var Q1;
            Q1=makeQuery(id+"F22.opExtrude","CAP_EDGE",EDGE,{"disambiguationData":[OSD([sQuery(id+"F21.wireOp",EDGE,"E81.0.1")])],"isStart":false});
            var Q2;
            Q2=makeQuery(id+"F20.opExtrude","CAP_EDGE",EDGE,{"disambiguationData":[OSD([sQuery(id+"F19.wireOp",EDGE,"E79.0.5")])],"isStart":false});
            var Q3;
            Q3=makeQuery(id+"F22.opExtrude","CAP_EDGE",EDGE,{"disambiguationData":[OSD([sQuery(id+"F21.wireOp",EDGE,"E81.0.3")])],"isStart":false});
            fillet(context, id + "F23", {"entities" : qUnion([Q0, Q1, Q2, Q3]), "radius" : 3 * mm, "tangentPropagation" : true, "allowEdgeOverflow" : false});
        }
        {
            var Q0;
            Q0=makeQuery(id+"F13.boolean.opBoolean","MERGE",FACE,{"derivedFrom":[makeQuery(id+"F11.boolean.opBoolean","MERGE",FACE,{"derivedFrom":[makeQuery(id+"F9.opExtrude","SWEPT_FACE",FACE,{"disambiguationData":[OSD([sQuery(id+"F8.wireOp",EDGE,"E55")])]}),makeQuery(id+"F11.opExtrude","SWEPT_FACE",FACE,{"disambiguationData":[OSD([sQuery(id+"F10.wireOp",EDGE,"E57.0.1")])]})]}),makeQuery(id+"F13.opExtrude","SWEPT_FACE",FACE,{"disambiguationData":[OSD([sQuery(id+"F12.wireOp",EDGE,"E59.0.7")])]})]});
            var sketch = newSketch(context, id + "F24", { "sketchPlane" : qUnion([Q0])});
            skCircle(sketch, "E83", {"center": v(-0.51, -25.05) * mm, "radius": 21.68 * mm});
            skPoint(sketch, "E83.first.point", {"position": v(-17.1, -11.1) * mm});
            skPoint(sketch, "E83.second.point", {"position": v(16, -39.12) * mm});
            skPoint(sketch, "E83.third.point", {"position": v(20.88, -28.58) * mm});
            skCircle(sketch, "E84", {"center": v(-0.51, -25.05) * mm, "radius": 19.55 * mm});
            skCircle(sketch, "E85", {"center": v(-0.51, -25.05) * mm, "radius": 5.68 * mm});
            skFitSpline(sketch, "E86", {"points": [v(-8.64, -23.41) * mm, v(-10.34, -22.66) * mm, v(-12.69, -25.2) * mm, v(-15.41, -23.98) * mm, v(-16.35, -23.98) * mm, v(-14.57, -26.8) * mm, v(-13.06, -28.58) * mm, v(-11.56, -29.34) * mm, v(-10.15, -28.2) * mm, v(-9.96, -27.55) * mm, v(-8.27, -27.74) * mm, v(-7.8, -29.15) * mm, v(-8.64, -30) * mm, v(-9.2, -30.84) * mm, v(-9.2, -32.63) * mm, v(-10.43, -33.85) * mm, v(-13.25, -35.17) * mm, v(-9.68, -36.01) * mm, v(-7.42, -36.01) * mm, v(-5.92, -35.26) * mm, v(-5.73, -32.72) * mm, v(-3.85, -32.44) * mm, v(-3.1, -33.29) * mm, v(-3.57, -34.13) * mm, v(-3.28, -35.45) * mm, v(-1.97, -37.05) * mm, v(-1.22, -38.27) * mm, v(-2.72, -39.96) * mm, v(-2.81, -41.28) * mm, v(0, -39.59) * mm, v(2.64, -36.86) * mm, v(1.7, -35.82) * mm, v(1.13, -34.7) * mm, v(1.13, -33.76) * mm, v(1.89, -32.9) * mm, v(2.54, -32.35) * mm, v(3.3, -33.47) * mm, v(4.05, -34.32) * mm, v(5.18, -35.07) * mm, v(6.4, -34.41) * mm, v(7.06, -34.13) * mm, v(7.72, -35.45) * mm, v(8.28, -36.86) * mm, v(8.75, -37.99) * mm, v(9.6, -36.58) * mm, v(9.6, -35.26) * mm, v(9.88, -33.85) * mm, v(10.16, -32.9) * mm, v(9.88, -31.88) * mm, v(9.31, -30.75) * mm, v(8.66, -31.22) * mm, v(8, -31.03) * mm, v(7.15, -30.75) * mm, v(6.4, -30.09) * mm, v(6.21, -28.96) * mm, v(6.96, -27.83) * mm, v(8, -28.4) * mm, v(9.78, -28.11) * mm, v(10.44, -26.9) * mm, v(11.85, -26.6) * mm, v(13.45, -26.99) * mm, v(14.58, -27.64) * mm, v(15.33, -28.02) * mm, v(15.05, -27.08) * mm, v(13.83, -25.3) * mm, v(12.6, -23.04) * mm, v(11.1, -22.28) * mm, v(9.4, -22.38) * mm, v(8.56, -23.6) * mm, v(7.81, -23.79) * mm, v(6.68, -22.85) * mm, v(7.34, -21.72) * mm, v(8.47, -20.6) * mm, v(8.47, -19) * mm, v(8.66, -17.68) * mm, v(10.82, -16.83) * mm, v(12.04, -16.08) * mm, v(9.13, -15.51) * mm, v(7.25, -15.14) * mm, v(5.46, -15.6) * mm, v(4.14, -16.08) * mm, v(4.8, -17.2) * mm, v(4.52, -18.43) * mm, v(3.01, -18.43) * mm, v(1.98, -17.68) * mm, v(2.54, -17.02) * mm, v(1.98, -15.51) * mm, v(0.76, -13.92) * mm, v(0, -13.45) * mm, v(0, -11.85) * mm, v(1.98, -9.87) * mm, v(1.98, -9.3) * mm, v(0, -10.25) * mm, v(-1.78, -11.57) * mm, v(-2.9, -12.88) * mm, v(-3.94, -14.1) * mm, v(-3, -15.42) * mm, v(-2.25, -16.55) * mm, v(-2.63, -17.58) * mm, v(-3.47, -18.34) * mm, v(-3.85, -18.62) * mm, v(-5.17, -17.2) * mm, v(-6.2, -16.17) * mm, v(-7.7, -16.74) * mm, v(-8.36, -17.2) * mm, v(-9.2, -16.17) * mm, v(-9.68, -15.42) * mm, v(-9.87, -14.3) * mm, v(-10.24, -12.79) * mm, v(-11.28, -15.33) * mm, v(-11.28, -18.8) * mm, v(-10.9, -20.03) * mm, v(-9.02, -20.3) * mm, v(-8.08, -20.69) * mm, v(-7.8, -21.81) * mm, v(-7.8, -22.75) * mm, v(-8.64, -23.41) * mm]});
            skCircle(sketch, "E87", {"center": v(-0.51, -25.05) * mm, "radius": 6.46 * mm});
            skCircle(sketch, "E88", {"center": v(45.15, -59.78) * mm, "radius": 21.6 * mm});
            skPoint(sketch, "E88.first.point", {"position": v(25.11, -51.71) * mm});
            skPoint(sketch, "E88.second.point", {"position": v(63, -71.93) * mm});
            skPoint(sketch, "E88.third.point", {"position": v(58.11, -42.5) * mm});
            skCircle(sketch, "E89", {"center": v(45.15, -59.78) * mm, "radius": 19.53 * mm});
            skFitSpline(sketch, "E90", {"points": [v(46.55, -44.85) * mm, v(44.3, -46.73) * mm, v(41.66, -49.93) * mm, v(39.6, -52.84) * mm, v(37.8, -55.66) * mm, v(36.49, -58.77) * mm, v(35.92, -61.87) * mm, v(36.2, -65.63) * mm, v(37.8, -68.55) * mm, v(39.69, -70.33) * mm, v(42.88, -72.12) * mm, v(47.02, -72.02) * mm, v(50.12, -70.14) * mm, v(52.38, -66.85) * mm, v(52.85, -63.47) * mm, v(52.38, -60.84) * mm, v(50.97, -58.2) * mm, v(49, -55.95) * mm, v(47.4, -53.31) * mm, v(46.55, -51.62) * mm, v(46.55, -44.85) * mm]});
            skFitSpline(sketch, "E91", {"points": [v(48.9, -58.48) * mm, v(48.71, -60.84) * mm, v(48.05, -62.53) * mm, v(47.87, -63.84) * mm, v(48.71, -64.88) * mm, v(50.12, -64.6) * mm, v(50.69, -63.28) * mm, v(50.69, -61.68) * mm, v(50.12, -60.84) * mm, v(48.9, -58.48) * mm]});
            skCircle(sketch, "E92", {"center": v(-45.8, -58.45) * mm, "radius": 21.74 * mm});
            skPoint(sketch, "E92.first.point", {"position": v(-60.26, -42.22) * mm});
            skPoint(sketch, "E92.second.point", {"position": v(-32.43, -75.6) * mm});
            skPoint(sketch, "E92.third.point", {"position": v(-31.02, -42.5) * mm});
            skCircle(sketch, "E93", {"center": v(-45.8, -58.45) * mm, "radius": 19.78 * mm});
            skFitSpline(sketch, "E94", {"points": [v(-54.44, -62.72) * mm, v(-55.56, -63.75) * mm, v(-57.54, -64.22) * mm, v(-59.14, -63.56) * mm, v(-60.17, -62.62) * mm, v(-60.64, -60.74) * mm, v(-60.36, -58.95) * mm, v(-59.42, -58.01) * mm, v(-59.89, -57.07) * mm, v(-60.26, -56.32) * mm, v(-59.98, -54.07) * mm, v(-58.95, -52.84) * mm, v(-58.2, -52.65) * mm, v(-57.44, -50.5) * mm, v(-57.35, -49.55) * mm, v(-57.44, -48.33) * mm, v(-55.75, -45.98) * mm, v(-53.78, -45.7) * mm, v(-52.37, -46.07) * mm, v(-51.52, -46.36) * mm, v(-51.05, -44.76) * mm, v(-48.42, -43.35) * mm, v(-46.16, -42.6) * mm, v(-43.15, -43.53) * mm, v(-41.93, -44.66) * mm, v(-38.92, -44.66) * mm, v(-36.95, -45.7) * mm, v(-35.91, -47.3) * mm, v(-35.63, -48.7) * mm, v(-34.78, -48.8) * mm, v(-33.37, -49.83) * mm, v(-33.84, -51.06) * mm, v(-32.62, -52.1) * mm, v(-31.4, -53.6) * mm, v(-31.21, -56.42) * mm, v(-31.96, -57.73) * mm, v(-30.74, -58.3) * mm, v(-30.55, -60.27) * mm, v(-31.87, -61.78) * mm, v(-34.03, -62.25) * mm, v(-35.63, -60.93) * mm, v(-37.42, -60.65) * mm, v(-40.33, -61.3) * mm, v(-41.84, -62.43) * mm, v(-42.4, -64.5) * mm, v(-42.68, -66.66) * mm, v(-42.12, -68.26) * mm, v(-40.33, -69.3) * mm, v(-37.6, -69.2) * mm, v(-36.66, -69.77) * mm, v(-36.48, -70.24) * mm, v(-37.23, -70.43) * mm, v(-38.26, -70.52) * mm, v(-37.6, -71.18) * mm, v(-38.26, -71.65) * mm, v(-38.73, -72.12) * mm, v(-39.77, -71.65) * mm, v(-41.27, -71.46) * mm, v(-41.18, -72.3) * mm, v(-41.74, -72.68) * mm, v(-42.59, -72.59) * mm, v(-44.28, -71.37) * mm, v(-45.78, -72.78) * mm, v(-46.44, -72.59) * mm, v(-47.1, -70.99) * mm, v(-47.67, -70.99) * mm, v(-48.42, -72.5) * mm, v(-49.17, -72.5) * mm, v(-49.83, -70.8) * mm, v(-54.62, -70.43) * mm, v(-51.9, -68.45) * mm, v(-49.55, -67.89) * mm, v(-48.6, -67.13) * mm, v(-48.6, -64.88) * mm, v(-50.2, -63.19) * mm, v(-51.9, -62.25) * mm, v(-52.55, -61.78) * mm, v(-54.44, -62.72) * mm]});
            skFitSpline(sketch, "E95", {"points": [v(-52.74, -59.05) * mm, v(-51.05, -59.42) * mm, v(-50.02, -60.27) * mm, v(-48.7, -60.93) * mm, v(-48.04, -60.84) * mm, v(-48.89, -59.61) * mm, v(-50.77, -58.58) * mm, v(-52, -58.4) * mm, v(-52.74, -59.05) * mm]});
            skFitSpline(sketch, "E96", {"points": [v(-49.55, -56.13) * mm, v(-49.36, -55.2) * mm, v(-50.58, -54.82) * mm, v(-51.33, -55.38) * mm, v(-51.33, -55.85) * mm, v(-50.49, -55.76) * mm, v(-49.55, -56.13) * mm]});
            skFitSpline(sketch, "E97", {"points": [v(-46.44, -54.54) * mm, v(-46.35, -53.22) * mm, v(-47.48, -52.65) * mm, v(-47.57, -53.5) * mm, v(-46.44, -54.54) * mm]});
            skFitSpline(sketch, "E98", {"points": [v(-42.68, -56.23) * mm, v(-42.59, -52.94) * mm, v(-41.37, -53.5) * mm, v(-40.99, -54.54) * mm, v(-41.65, -55.57) * mm, v(-42.68, -56.23) * mm]});
            skFitSpline(sketch, "E99", {"points": [v(-42.12, -59.61) * mm, v(-40.9, -58.3) * mm, v(-39.58, -58.01) * mm, v(-38.83, -58.3) * mm, v(-39.3, -58.95) * mm, v(-40.61, -59.33) * mm, v(-42.12, -59.61) * mm]});
            skCircle(sketch, "E100", {"center": v(-29.42, -112.88) * mm, "radius": 21.64 * mm});
            skPoint(sketch, "E100.first.point", {"position": v(-45.88, -98.82) * mm});
            skPoint(sketch, "E100.second.point", {"position": v(-14.29, -128.35) * mm});
            skPoint(sketch, "E100.third.point", {"position": v(-13.9, -97.79) * mm});
            skCircle(sketch, "E101", {"center": v(-29.42, -112.88) * mm, "radius": 19.68 * mm});
            skFitSpline(sketch, "E102", {"points": [v(-22.47, -124.96) * mm, v(-24.16, -125.8) * mm, v(-25.95, -126.18) * mm, v(-29.42, -126.75) * mm, v(-32.25, -126.65) * mm, v(-34.97, -126.65) * mm, v(-36.76, -126.09) * mm, v(-39.1, -125.15) * mm, v(-40.61, -123.36) * mm, v(-41.65, -121.2) * mm, v(-41.46, -116.6) * mm, v(-40.52, -114.52) * mm, v(-38.73, -112.55) * mm, v(-36.29, -111.33) * mm, v(-33.56, -111.33) * mm, v(-31.77, -111.99) * mm, v(-29.42, -111.6) * mm, v(-26.7, -110.57) * mm, v(-24.91, -108.88) * mm, v(-24.53, -110.67) * mm, v(-25.29, -112.88) * mm, v(-26.7, -115) * mm, v(-28.3, -116.03) * mm, v(-29.42, -117.25) * mm, v(-29.42, -118.1) * mm, v(-28.39, -118.66) * mm, v(-26.42, -118.38) * mm, v(-25.29, -117.53) * mm, v(-24.44, -115.37) * mm, v(-24.35, -113.68) * mm, v(-24.35, -112.88) * mm, v(-23.88, -111.33) * mm, v(-23.5, -110.1) * mm, v(-22.47, -110.01) * mm, v(-22.65, -111.42) * mm, v(-22.94, -112.88) * mm, v(-22.56, -113.58) * mm, v(-21.24, -111.42) * mm, v(-20.68, -110.01) * mm, v(-21.34, -109.16) * mm, v(-23.03, -108.79) * mm, v(-25.2, -107) * mm, v(-25.85, -105.03) * mm, v(-25.66, -103.62) * mm, v(-24.16, -105.78) * mm, v(-23.88, -106.34) * mm, v(-23.5, -105.12) * mm, v(-23.31, -104) * mm, v(-24.06, -102.58) * mm, v(-25.48, -101.55) * mm, v(-26.32, -101.45) * mm, v(-27.17, -101.83) * mm, v(-28.2, -102.4) * mm, v(-29.42, -102.77) * mm, v(-31.5, -102.49) * mm, v(-32.53, -101.74) * mm, v(-31.02, -101.27) * mm, v(-29.42, -100.9) * mm, v(-29.42, -100.42) * mm, v(-29.42, -99.86) * mm, v(-31.21, -99.39) * mm, v(-32.34, -99) * mm, v(-34.03, -99.1) * mm, v(-35.25, -98.92) * mm, v(-35.54, -98.07) * mm, v(-33.84, -98.07) * mm, v(-33.37, -97.5) * mm, v(-30.36, -97.79) * mm, v(-28.48, -97.98) * mm, v(-26.5, -98.45) * mm, v(-25.1, -99) * mm, v(-23.4, -99.95) * mm, v(-22.1, -100.9) * mm, v(-20.77, -102.02) * mm, v(-19.83, -103.71) * mm, v(-18.52, -105.5) * mm, v(-18.33, -107.57) * mm, v(-17.67, -106.16) * mm, v(-17.95, -104.75) * mm, v(-18.42, -103.43) * mm, v(-19.36, -101.55) * mm, v(-18.52, -102.3) * mm, v(-17.48, -103.62) * mm, v(-16.64, -105.5) * mm, v(-15.6, -108.6) * mm, v(-15.5, -110.76) * mm, v(-16.17, -112.88) * mm, v(-17.3, -115) * mm, v(-18.42, -116.22) * mm, v(-19.55, -117.63) * mm, v(-20.5, -118.47) * mm, v(-21.34, -119.13) * mm, v(-20.5, -119.04) * mm, v(-18.7, -118.57) * mm, v(-17.58, -117.63) * mm, v(-16.07, -116.69) * mm, v(-15.5, -116.31) * mm, v(-15.88, -118.57) * mm, v(-16.73, -119.88) * mm, v(-17.76, -121.2) * mm, v(-19.83, -122.14) * mm, v(-21.71, -122.52) * mm, v(-23.78, -122.42) * mm, v(-25.38, -122.8) * mm, v(-26.8, -123.36) * mm, v(-27.54, -123.83) * mm, v(-26.42, -124.3) * mm, v(-24.82, -124.58) * mm, v(-22.47, -124.96) * mm]});
            skFitSpline(sketch, "E103", {"points": [v(-38.54, -104.56) * mm, v(-38.92, -103.43) * mm, v(-39.2, -103.15) * mm, v(-39.96, -103.62) * mm, v(-40.61, -104.37) * mm, v(-41.18, -103.62) * mm, v(-40.33, -102.4) * mm, v(-39.4, -100.98) * mm, v(-37.8, -99.86) * mm, v(-36.1, -99.57) * mm, v(-35.25, -100.04) * mm, v(-34.6, -101.45) * mm, v(-34.6, -102.4) * mm, v(-35.25, -102.4) * mm, v(-36.48, -102.4) * mm, v(-37.23, -103.33) * mm, v(-38.54, -104.56) * mm]});
            skFitSpline(sketch, "E104", {"points": [v(-33.28, -103.62) * mm, v(-31.87, -105.6) * mm, v(-31.77, -106.06) * mm, v(-30.18, -107) * mm, v(-28.2, -106.81) * mm, v(-27.07, -105.87) * mm, v(-27.17, -104.18) * mm, v(-28.2, -103.71) * mm, v(-29.42, -103.62) * mm, v(-30.27, -104.46) * mm, v(-30.83, -104.65) * mm, v(-31.59, -104) * mm, v(-33.28, -103.62) * mm]});
            skCircle(sketch, "E105", {"center": v(27.51, -112.88) * mm, "radius": 21.75 * mm});
            skPoint(sketch, "E105.first.point", {"position": v(12.32, -97.32) * mm});
            skPoint(sketch, "E105.second.point", {"position": v(43.26, -127.88) * mm});
            skPoint(sketch, "E105.third.point", {"position": v(42.5, -97.13) * mm});
            skCircle(sketch, "E106", {"center": v(27.51, -112.88) * mm, "radius": 19.82 * mm});
            skFitSpline(sketch, "E107", {"points": [v(18.44, -101.64) * mm, v(16.27, -103.71) * mm, v(15.05, -105.78) * mm, v(14.02, -107.66) * mm, v(13.45, -109.92) * mm, v(13.26, -112.55) * mm, v(13.92, -114.9) * mm, v(15.9, -116.69) * mm, v(18.34, -117.44) * mm, v(20.32, -117.44) * mm, v(21.16, -117.9) * mm, v(21.26, -118.85) * mm, v(21.54, -120.45) * mm, v(21.16, -121.67) * mm, v(21.16, -123.55) * mm, v(20.7, -124.2) * mm, v(20.97, -124.77) * mm, v(21.26, -125.9) * mm, v(21.82, -126.84) * mm, v(23.32, -127.22) * mm, v(23.6, -125.24) * mm, v(23.7, -124.02) * mm, v(23.89, -123.08) * mm, v(24.45, -123.36) * mm, v(24.92, -124.96) * mm, v(25.11, -126.37) * mm, v(26.7, -126.47) * mm, v(27.18, -125.9) * mm, v(27, -123.36) * mm, v(27.56, -122.7) * mm, v(27.84, -122.42) * mm, v(28.12, -123.36) * mm, v(28.12, -125.15) * mm, v(28.3, -125.71) * mm, v(29.15, -125.34) * mm, v(30.19, -124.77) * mm, v(30.38, -124.2) * mm, v(30.47, -123.17) * mm, v(30.56, -122.8) * mm, v(30.94, -122.8) * mm, v(31.32, -123.74) * mm, v(31.5, -124.68) * mm, v(31.6, -125.43) * mm, v(30.94, -125.71) * mm, v(31.13, -126.47) * mm, v(31.5, -127.03) * mm, v(31.5, -127.78) * mm, v(32.44, -127.31) * mm, v(33.2, -127.31) * mm, v(33.86, -127.31) * mm, v(33.86, -125.9) * mm, v(34.14, -125.43) * mm, v(33.48, -125.05) * mm, v(34.04, -124.68) * mm, v(33.67, -123.93) * mm, v(33.67, -122.61) * mm, v(33.76, -118.38) * mm, v(34.89, -117.72) * mm, v(36.4, -117.25) * mm, v(38.27, -116.87) * mm, v(39.97, -116.5) * mm, v(41.28, -115.09) * mm, v(41.85, -113.3) * mm, v(41.57, -110.2) * mm, v(40.9, -107.38) * mm, v(39.69, -105.22) * mm, v(38.27, -103.43) * mm, v(36.77, -102.02) * mm, v(35.92, -102.86) * mm, v(34.33, -103.33) * mm, v(32.82, -103.52) * mm, v(34.42, -102.58) * mm, v(35.17, -101.83) * mm, v(35.74, -100.7) * mm, v(34.33, -99.95) * mm, v(32.35, -99) * mm, v(30.38, -98.82) * mm, v(28.5, -98.45) * mm, v(25.3, -98.45) * mm, v(23.51, -98.82) * mm, v(20.97, -99.39) * mm, v(19.85, -100.33) * mm, v(19.75, -101.55) * mm, v(20.03, -102.68) * mm, v(20.97, -103.71) * mm, v(21.82, -104.75) * mm, v(22.57, -105.5) * mm, v(21.07, -105.03) * mm, v(19.75, -104.56) * mm, v(19.28, -104) * mm, v(19, -102.96) * mm, v(18.44, -101.64) * mm]});
            skFitSpline(sketch, "E108", {"points": [v(24.92, -111.7) * mm, v(23.8, -110.01) * mm, v(22, -109.07) * mm, v(20.22, -108.5) * mm, v(18.81, -108.7) * mm, v(16.93, -110.01) * mm, v(16.18, -111.52) * mm, v(16, -112.83) * mm, v(16.37, -113.4) * mm, v(17.5, -114.24) * mm, v(19, -114.52) * mm, v(21.16, -114.9) * mm, v(22.67, -114.62) * mm, v(24.17, -113.96) * mm, v(25.02, -113.11) * mm, v(24.92, -111.7) * mm]});
            skFitSpline(sketch, "E109", {"points": [v(32.16, -109.54) * mm, v(33.57, -108.7) * mm, v(34.51, -108.41) * mm, v(36.49, -108.7) * mm, v(37.9, -109.45) * mm, v(38.46, -110.3) * mm, v(39.12, -111.33) * mm, v(39.4, -112.55) * mm, v(38.93, -114.05) * mm, v(37.52, -114.8) * mm, v(35.74, -114.9) * mm, v(33.86, -114.71) * mm, v(31.32, -114.62) * mm, v(30.56, -114.24) * mm, v(30.56, -112.27) * mm, v(30.85, -110.76) * mm, v(32.16, -109.54) * mm]});
            skFitSpline(sketch, "E110", {"points": [v(26.43, -114.24) * mm, v(25.77, -116.03) * mm, v(25.49, -117.06) * mm, v(25.3, -118.57) * mm, v(25.4, -120.17) * mm, v(26.33, -120.35) * mm, v(27.84, -120.54) * mm, v(29.15, -120.35) * mm, v(29.44, -120.35) * mm, v(29.81, -119.5) * mm, v(29.9, -118) * mm, v(29.53, -116.69) * mm, v(28.68, -114.9) * mm, v(28.03, -114.05) * mm, v(28.12, -117.16) * mm, v(27.74, -118.66) * mm, v(27.37, -119.13) * mm, v(27, -119.13) * mm, v(27, -117.53) * mm, v(27.09, -115.28) * mm, v(26.43, -114.24) * mm]});
            skSolve(sketch);
        }
        {
            var Q0;
            Q0=makeQuery(id+"F24.imprint","IMPRINT",FACE,{"disambiguationData":[TD([[makeQuery(id+"F24.imprint","IMPRINT",EDGE,{"derivedFrom":sQuery(id+"F24.wireOp",EDGE,"E85")}),1.0]])]});
            var Q1;
            Q1=makeQuery(id+"F24.imprint","IMPRINT",FACE,{"disambiguationData":[TD([[makeQuery(id+"F24.imprint","IMPRINT",EDGE,{"derivedFrom":sQuery(id+"F24.wireOp",EDGE,"E86")}),1.0]])]});
            var Q2;
            Q2=makeQuery(id+"F24.imprint","IMPRINT",FACE,{"disambiguationData":[TD([[makeQuery(id+"F24.imprint","IMPRINT",EDGE,{"derivedFrom":sQuery(id+"F24.wireOp",EDGE,"E83")}),1.0]])]});
            var Q3;
            Q3=makeQuery(id+"F24.imprint","IMPRINT",FACE,{"disambiguationData":[TD([[makeQuery(id+"F24.imprint","IMPRINT",EDGE,{"derivedFrom":sQuery(id+"F24.wireOp",EDGE,"E92")}),1.0]])]});
            var Q4;
            Q4=makeQuery(id+"F24.imprint","IMPRINT",FACE,{"disambiguationData":[TD([[makeQuery(id+"F24.imprint","IMPRINT",EDGE,{"derivedFrom":sQuery(id+"F24.wireOp",EDGE,"E94")}),-1.0]])]});
            var Q5;
            Q5=makeQuery(id+"F24.imprint","IMPRINT",FACE,{"disambiguationData":[TD([[makeQuery(id+"F24.imprint","IMPRINT",EDGE,{"derivedFrom":sQuery(id+"F24.wireOp",EDGE,"E88")}),1.0]])]});
            var Q6;
            Q6=makeQuery(id+"F24.imprint","IMPRINT",FACE,{"disambiguationData":[TD([[makeQuery(id+"F24.imprint","IMPRINT",EDGE,{"derivedFrom":sQuery(id+"F24.wireOp",EDGE,"E90")}),1.0]])]});
            var Q7;
            Q7=makeQuery(id+"F24.imprint","IMPRINT",FACE,{"disambiguationData":[TD([[makeQuery(id+"F24.imprint","IMPRINT",EDGE,{"derivedFrom":sQuery(id+"F24.wireOp",EDGE,"E100")}),1.0]])]});
            var Q8;
            Q8=makeQuery(id+"F24.imprint","IMPRINT",FACE,{"disambiguationData":[TD([[makeQuery(id+"F24.imprint","IMPRINT",EDGE,{"derivedFrom":sQuery(id+"F24.wireOp",EDGE,"E102")}),-1.0]])]});
            var Q9;
            Q9=makeQuery(id+"F24.imprint","IMPRINT",FACE,{"disambiguationData":[TD([[makeQuery(id+"F24.imprint","IMPRINT",EDGE,{"derivedFrom":sQuery(id+"F24.wireOp",EDGE,"E103")}),-1.0]])]});
            var Q10;
            Q10=makeQuery(id+"F24.imprint","IMPRINT",FACE,{"disambiguationData":[TD([[makeQuery(id+"F24.imprint","IMPRINT",EDGE,{"derivedFrom":sQuery(id+"F24.wireOp",EDGE,"E104")}),1.0]])]});
            var Q11;
            Q11=makeQuery(id+"F24.imprint","IMPRINT",FACE,{"disambiguationData":[TD([[makeQuery(id+"F24.imprint","IMPRINT",EDGE,{"derivedFrom":sQuery(id+"F24.wireOp",EDGE,"E105")}),1.0]])]});
            var Q12;
            Q12=makeQuery(id+"F24.imprint","IMPRINT",FACE,{"disambiguationData":[TD([[makeQuery(id+"F24.imprint","IMPRINT",EDGE,{"derivedFrom":sQuery(id+"F24.wireOp",EDGE,"E107")}),1.0]])]});
            extrude(context, id + "F25", {"entities" : qUnion([Q0, Q1, Q2, Q3, Q4, Q5, Q6, Q7, Q8, Q9, Q10, Q11, Q12]), "operationType" : NewBodyOperationType.REMOVE, "oppositeDirection" : true, "depth" : 2.5 * mm, "offsetDistance" : 25 * mm});
        }
    });
